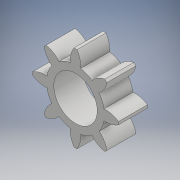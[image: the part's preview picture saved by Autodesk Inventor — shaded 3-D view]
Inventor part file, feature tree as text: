
AUTODESK INVENTOR PART (.ipt)
format: ipt  version: 2018 (Build 220112000, 112)  size: 158,208 bytes
history: native  units: mm
features: extrude x2, sketch x2, pattern_circular x1
ambient origin geometry x8: Origin, YZ Plane, XZ Plane, XY Plane, X Axis, Y Axis, Z Axis, Center Point
bodies: Solid1 (feature_tree)
feature tree (5):
  extrude  "Extrusion1"  Depth=4.0mm
  extrude  "Extrusion2"  Depth=2.0mm
  pattern_circular  "Circular Pattern1"  [2 undecoded]
  sketch  "Sketch1"  dims[d0=3.0mm d1=4.0mm]
  sketch  "Sketch2"  dims[d2=2.0mm d3=0.0mm d4=0.2mm d5=0.35mm d6=90.0deg d7=0.7mm d8=1.541mm d9=2.0mm d10=0.0mm d11=80.0mm d12=360.0deg]
note: 2 required parameter values undecoded (feature->parameter linkage not recoverable at this tier; creation-order binding heuristic only, values carry confidence <= 0.55)
